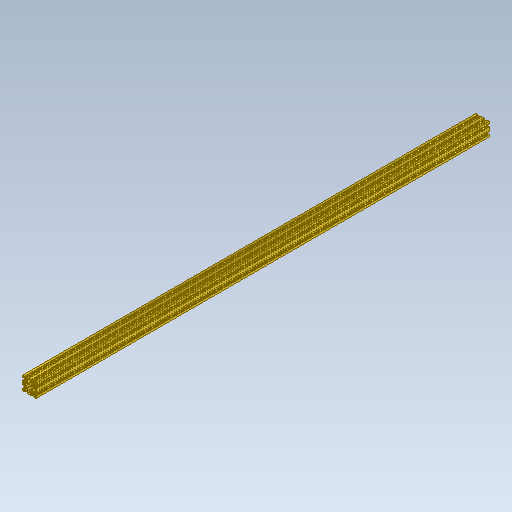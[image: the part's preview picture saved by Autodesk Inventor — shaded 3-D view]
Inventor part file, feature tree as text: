
AUTODESK INVENTOR PART (.ipt)
format: ipt  version: 2025.2 (Build 292293000, 293)  size: 440,832 bytes
history: native  units: mm
features: mirror x2, sketch x2, other x1, extrude x1
ambient origin geometry x8: Origin, YZ Plane, XZ Plane, XY Plane, X Axis, Y Axis, Z Axis, Center Point
bodies: Body1 (feature_tree)
feature tree (6):
  other  "Sólido1"
  extrude  "Extrusão1"  Depth=60.0mm
  mirror  "Espelhar1"
  mirror  "Espelhar2"
  sketch  "Esboço1"  dims[d0=30.0mm d1=60.0mm]
  sketch  "Esboço - Padrão circular1"  dims[d3=15.0mm d4=15.0mm d5=10.0mm d6=8.0mm d7=8.2mm d8=0.5mm d9=0.5mm d10=1.1mm d12=2.2mm d14=26.5mm d15=4.5mm d16=1.1mm d18=2.2mm d19=1.1mm d21=2.2mm d22=40.0mm d24=360.0deg d26=2000.0mm d27=0.0mm]
